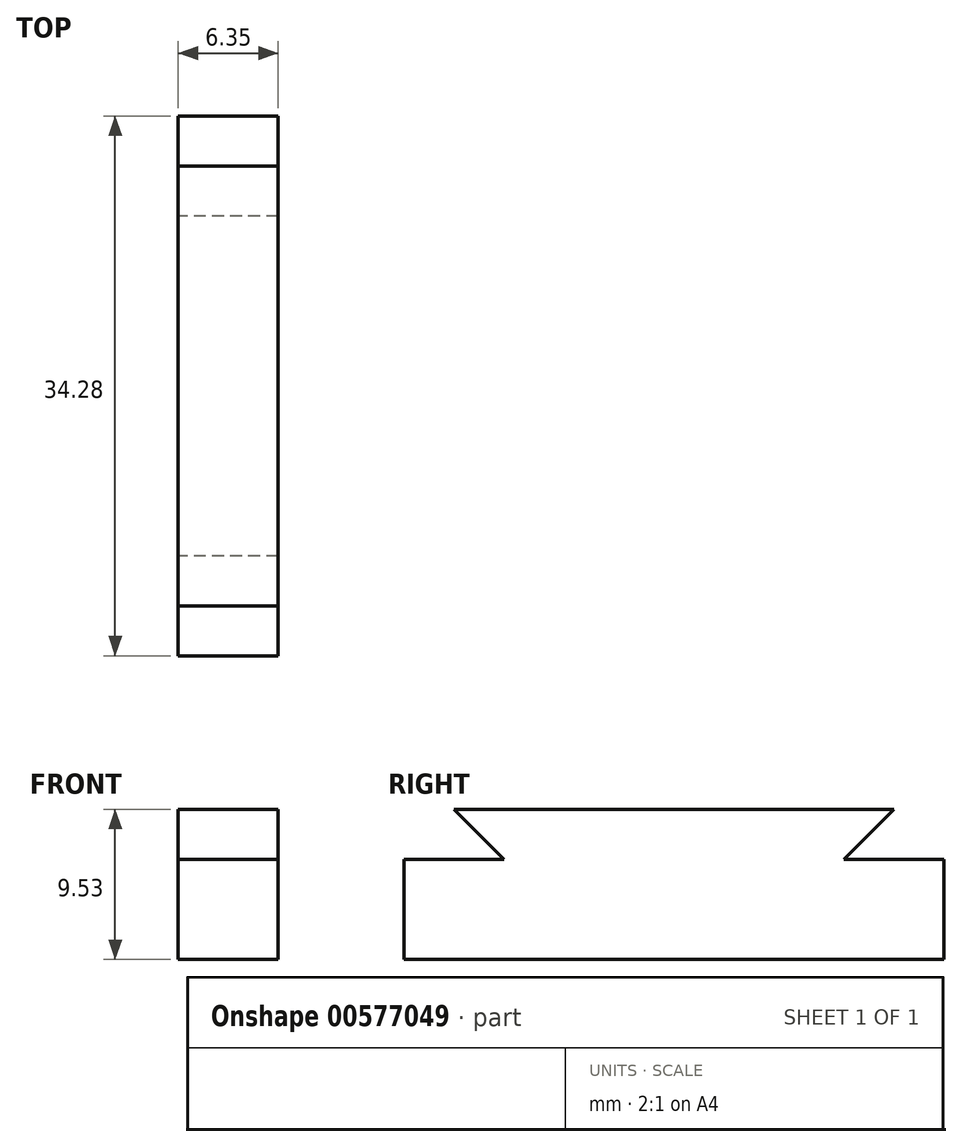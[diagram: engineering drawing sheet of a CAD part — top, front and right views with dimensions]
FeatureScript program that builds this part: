
annotation { "Feature Type Name" : "Feature", "Feature Type Description" : "" }
export const myFeature = defineFeature(function(context is Context, id is Id, definition is map)
    precondition{}
    {
        {
            var Q0;
            Q0=qCreatedBy(makeId("Top.planeOp"),FACE);
            var sketch = newSketch(context, id + "F0", { "sketchPlane" : qUnion([Q0])});
            skLineSegment(sketch, "E0.bottom", {"start": v(3.18, 17.15) * mm, "end": v(-3.18, 17.15) * mm});
            skLineSegment(sketch, "E0.top", {"start": v(3.17, -17.15) * mm, "end": v(-3.18, -17.15) * mm});
            skLineSegment(sketch, "E0.left", {"start": v(3.18, 17.15) * mm, "end": v(3.17, -17.15) * mm});
            skLineSegment(sketch, "E0.right", {"start": v(-3.17, 17.15) * mm, "end": v(-3.18, -17.15) * mm});
            skPoint(sketch, "E0.middle", {"position": v(0, 0) * mm});
            skSolve(sketch);
        }
        {
            var Q0;
            Q0 = qSketchRegion(id + "F0", true);
            extrude(context, id + "F1", {"entities" : qUnion([Q0]), "depth" : 9.52 * mm, "offsetDistance" : 25.4 * mm});
        }
        {
            var Q0;
            Q0=makeQuery(id+"F1.opExtrude","SWEPT_FACE",FACE,{"disambiguationData":[OSD([sQuery(id+"F0.wireOp",EDGE,"E0.right")])]});
            var sketch = newSketch(context, id + "F2", { "sketchPlane" : qUnion([Q0])});
            skLineSegment(sketch, "E1", {"start": v(-17.15, 6.35) * mm, "end": v(-10.8, 6.35) * mm});
            skLineSegment(sketch, "E2.trimOffspring", {"start": v(10.8, 6.35) * mm, "end": v(17.14, 6.35) * mm});
            skLineSegment(sketch, "E3", {"start": v(-13.97, 9.53) * mm, "end": v(-10.8, 6.35) * mm});
            skLineSegment(sketch, "E4", {"start": v(13.97, 9.53) * mm, "end": v(10.8, 6.35) * mm});
            skSolve(sketch);
        }
        {
            var Q0;
            Q0 = qSketchRegion(id + "F2", true);
            var Q1;
            {var subQ0=sQuery(id+"F2.wireOp",EDGE,"E1");Q1=makeQuery(id+"F2.imprint","IMPRINT",FACE,{"disambiguationData":[TD([[makeQuery(id+"F2.imprint","IMPRINT",EDGE,{"derivedFrom":subQ0}),1.0]])]});}
            var Q2;
            {var subQ0=sQuery(id+"F2.wireOp",EDGE,"E2.trimOffspring");Q2=makeQuery(id+"F2.imprint","IMPRINT",FACE,{"disambiguationData":[TD([[makeQuery(id+"F2.imprint","IMPRINT",EDGE,{"derivedFrom":subQ0}),1.0]])]});}
            extrude(context, id + "F3", {"entities" : qUnion([Q0, Q1, Q2]), "operationType" : NewBodyOperationType.REMOVE, "endBound" : BoundingType.THROUGH_ALL, "oppositeDirection" : true, "depth" : 25.4 * mm, "offsetDistance" : 25.4 * mm});
        }
    });
